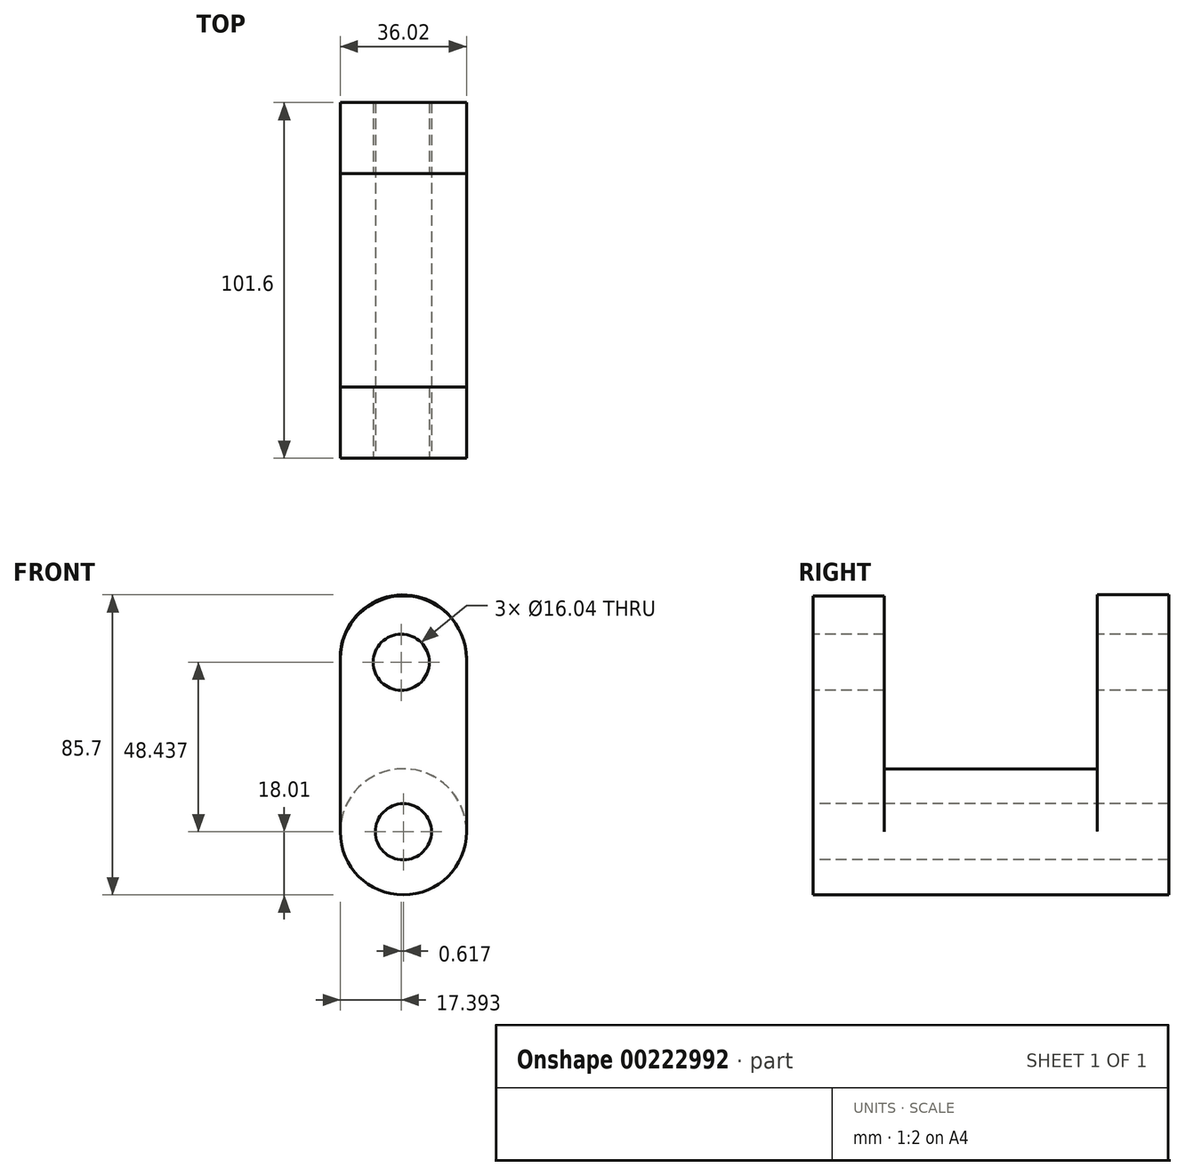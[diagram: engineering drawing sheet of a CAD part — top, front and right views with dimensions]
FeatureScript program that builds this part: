
annotation { "Feature Type Name" : "Feature", "Feature Type Description" : "" }
export const myFeature = defineFeature(function(context is Context, id is Id, definition is map)
    precondition{}
    {
        {
            var Q0;
            Q0=qCreatedBy(makeId("Front.planeOp"),FACE);
            var sketch = newSketch(context, id + "F0", { "sketchPlane" : qUnion([Q0])});
            skCircle(sketch, "E0", {"center": v(0, 0) * mm, "radius": 18.01 * mm});
            skSolve(sketch);
        }
        {
            var Q0;
            Q0 = qSketchRegion(id + "F0", true);
            extrude(context, id + "F1", {"entities" : qUnion([Q0]), "depth" : 50.8 * mm, "hasSecondDirection" : true, "secondDirectionOppositeDirection" : true, "secondDirectionDepth" : 50.8 * mm});
        }
        {
            var Q0;
            Q0=makeQuery(id+"F1.opExtrude","CAP_FACE",FACE,{"disambiguationData":[OSD([sQuery(id+"F0.wireOp",EDGE,"E0")])],"isStart":false});
            var sketch = newSketch(context, id + "F2", { "sketchPlane" : qUnion([Q0])});
            skLineSegment(sketch, "E1", {"start": v(-18.01, 0) * mm, "end": v(-18.01, 49.4) * mm});
            skLineSegment(sketch, "E2", {"start": v(-18.01, 49.4) * mm, "end": v(0, 49.4) * mm});
            skLineSegment(sketch, "E3", {"start": v(0, 49.4) * mm, "end": v(-18.01, 49.4) * mm});
            skLineSegment(sketch, "E4", {"start": v(-18.01, 0) * mm, "end": v(18.01, 0) * mm});
            skLineSegment(sketch, "E5", {"start": v(18.01, 0) * mm, "end": v(18.01, 49.4) * mm});
            skLineSegment(sketch, "E6", {"start": v(18.01, 49.4) * mm, "end": v(0, 49.4) * mm});
            skArc(sketch, "E7", {"start": v(-18.01, 0) * mm, "mid": v(0, -18.01) * mm, "end": v(18.01, 0) * mm});
            skArc(sketch, "E8", {"start": v(18.01, 49.4) * mm, "mid": v(0, 67.4) * mm, "end": v(-18.01, 49.4) * mm});
            skSolve(sketch);
        }
        {
            var Q0;
            Q0 = qSketchRegion(id + "F2", true);
            extrude(context, id + "F3", {"entities" : qUnion([Q0]), "operationType" : NewBodyOperationType.ADD, "oppositeDirection" : true, "depth" : 20.32 * mm});
        }
        {
            var Q0;
            Q0=makeQuery(id+"F1.opExtrude","CAP_FACE",FACE,{"disambiguationData":[OSD([sQuery(id+"F0.wireOp",EDGE,"E0")])],"isStart":true});
            var sketch = newSketch(context, id + "F4", { "sketchPlane" : qUnion([Q0])});
            skLineSegment(sketch, "E9", {"start": v(-18.01, 0) * mm, "end": v(18.01, 0) * mm});
            skLineSegment(sketch, "E10", {"start": v(18.01, 0) * mm, "end": v(18.01, 49.87) * mm});
            skLineSegment(sketch, "E11", {"start": v(18.01, 49.87) * mm, "end": v(-17.79, 49.87) * mm});
            skLineSegment(sketch, "E12", {"start": v(-17.79, 49.87) * mm, "end": v(-18.01, 0) * mm});
            skArc(sketch, "E13", {"start": v(18.01, 49.87) * mm, "mid": v(0.11, 67.7) * mm, "end": v(-17.79, 49.87) * mm});
            skSolve(sketch);
        }
        {
            var Q0;
            Q0 = qSketchRegion(id + "F4", true);
            extrude(context, id + "F5", {"entities" : qUnion([Q0]), "operationType" : NewBodyOperationType.ADD, "oppositeDirection" : true, "depth" : 20.32 * mm});
        }
        {
            var Q0;
            Q0=makeQuery(id+"F3.boolean.opBoolean","MERGE",FACE,{"derivedFrom":[makeQuery(id+"F1.opExtrude","CAP_FACE",FACE,{"disambiguationData":[OSD([sQuery(id+"F0.wireOp",EDGE,"E0")])],"isStart":false}),makeQuery(id+"F3.opExtrude","CAP_FACE",FACE,{"disambiguationData":[OSD([sQuery(id+"F2.wireOp",EDGE,"E1"),sQuery(id+"F2.wireOp",EDGE,"E5"),sQuery(id+"F2.wireOp",EDGE,"E7"),sQuery(id+"F2.wireOp",EDGE,"E8")])],"isStart":true})]});
            var sketch = newSketch(context, id + "F6", { "sketchPlane" : qUnion([Q0])});
            skCircle(sketch, "E14", {"center": v(0, 0) * mm, "radius": 8.02 * mm});
            skCircle(sketch, "E15", {"center": v(-0.62, 48.44) * mm, "radius": 8.02 * mm});
            skSolve(sketch);
        }
        {
            var Q0;
            Q0 = qSketchRegion(id + "F6", true);
            extrude(context, id + "F7", {"entities" : qUnion([Q0]), "operationType" : NewBodyOperationType.REMOVE, "endBound" : BoundingType.THROUGH_ALL, "oppositeDirection" : true, "depth" : 25.4 * mm});
        }
    });
